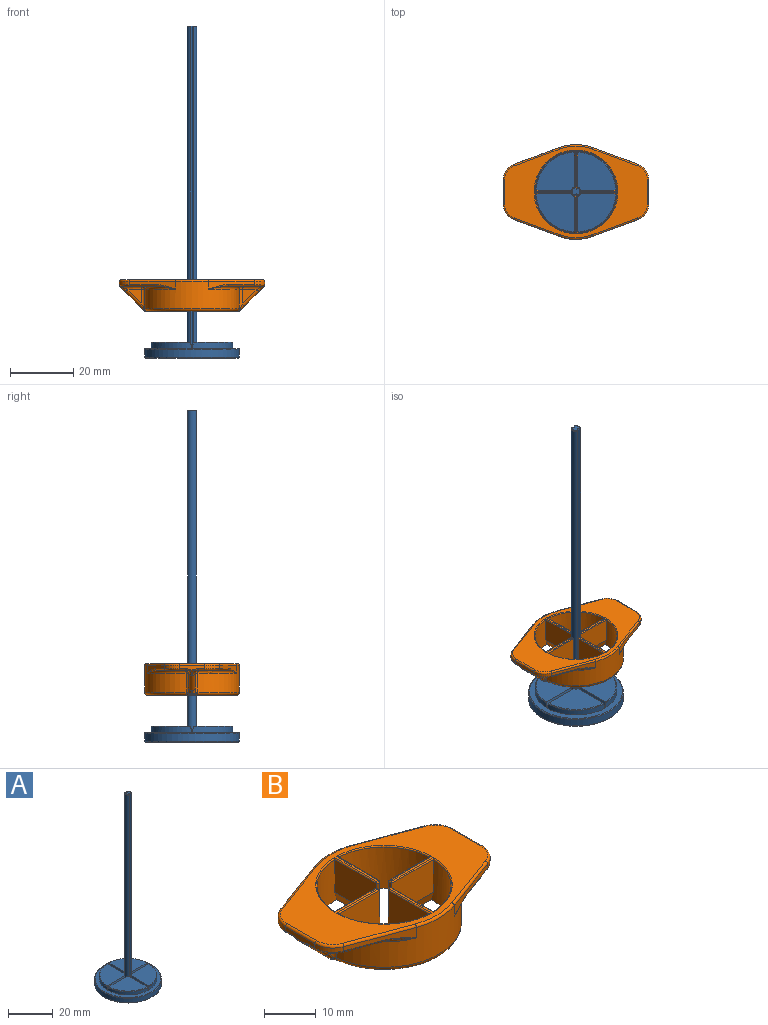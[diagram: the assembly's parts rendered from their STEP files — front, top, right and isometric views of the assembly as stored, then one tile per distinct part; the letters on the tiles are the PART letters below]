
ASSEMBLY  parts=2 mates=1
PART A: 44 faces, bbox 32.5x32.5x105 mm
  f0: cylinder r=15mm len=30mm, axis (0,0,-1), area 235.6mm2, adj f36,f43
  f1: plane 12.14x12.14mm, normal (0,0,1), area 112.7mm2, adj f8,f9,f14,f20,f32
  f2: plane 12.14x12.14mm, normal (0,0,1), area 112.7mm2, adj f6,f13,f15,f21,f34
  f3: plane 12.14x12.14mm, normal (0,0,1), area 112.7mm2, adj f5,f6,f17,f22,f35
  f4: plane 12.14x12.14mm, normal (0,0,1), area 112.7mm2, adj f9,f10,f18,f19,f33
  f5: plane 101.75x0.55mm, normal (0.71,0.71,0), area 78.7mm2, adj f3,f6,f10,f17,f38
  f6: cylinder r=1.5mm len=101.75mm, axis (0,0,-1), area 358.2mm2, adj f2,f3,f5,f7,f21,f22,f40
  f7: plane 103.75x0.55mm, normal (0.71,-0.71,0), area 79mm2, adj f6,f8,f13,f15,f16,f28,f42
  f8: plane 101.75x0.55mm, normal (-0.71,-0.71,0), area 78.7mm2, adj f1,f7,f9,f14,f41
  f9: cylinder r=1.5mm len=101.75mm, axis (0,0,-1), area 358.2mm2, adj f1,f4,f8,f10,f19,f20,f39
  f10: plane 101.75x0.55mm, normal (-0.71,0.71,0), area 78.7mm2, adj f4,f5,f9,f18,f37
  f11: plane 2.5x2.19mm, normal (0,0,1), area 3.9mm2, adj f37,f38,f39,f40,f41,f42
  f12: plane 29.5x29.5mm, normal (0,0,-1), area 140.2mm2, adj f30,f43
  f13: plane 12.06x2mm, normal (0.97,0,0.24), area 24.3mm2, adj f2,f7,f14,f16,f26,f34
  f14: plane 12.06x2mm, normal (-0.97,0,0.24), area 24.3mm2, adj f1,f8,f13,f24,f32
  f15: cylinder r=1.5mm len=4mm, axis (0,0,-1), area 0.2mm2, adj f2,f7,f16,f28
  f16: plane 4x0.07mm, normal (-1,0,0), area 0.3mm2, adj f7,f13,f15,f28
  f17: plane 12.06x2mm, normal (0.97,0,0.24), area 24.3mm2, adj f3,f5,f18,f25,f35
  f18: plane 12.06x2mm, normal (-0.97,0,0.24), area 24.3mm2, adj f4,f10,f17,f23,f33
  f19: plane 11.49x2mm, normal (0,-0.97,0.24), area 23.5mm2, adj f4,f9,f20,f23,f33
  f20: plane 11.49x2mm, normal (0,0.97,0.24), area 23.5mm2, adj f1,f9,f19,f24,f32
  f21: plane 11.49x2mm, normal (0,0.97,0.24), area 23.5mm2, adj f2,f6,f22,f26,f34
  f22: plane 11.49x2mm, normal (0,-0.97,0.24), area 23.5mm2, adj f3,f6,f21,f25,f35
  f23: cylinder r=12.9mm len=12.9mm, axis (0,0,-1), area 34.7mm2, adj f18,f19,f27,f33
  f24: cylinder r=12.9mm len=12.9mm, axis (0,0,-1), area 34.7mm2, adj f14,f20,f27,f32
  f25: cylinder r=12.9mm len=12.9mm, axis (0,0,-1), area 34.7mm2, adj f17,f22,f27,f35
  f26: cylinder r=12.9mm len=12.9mm, axis (0,0,-1), area 34.7mm2, adj f13,f21,f27,f34
  f27: plane 29.5x29.5mm, normal (0,0,1), area 160.7mm2, adj f23,f24,f25,f26,f36
  f28: plane 25.3x25.3mm, normal (0,0,-1), area 502.7mm2, adj f7,f15,f16,f31
  f29: cylinder r=12.9mm len=25.8mm, axis (0,0,-1), area 40.5mm2, adj f30,f31
  f30: torus R=13.15mm, axis (0,0,1), area 32.1mm2, adj f12,f29
  f31: torus R=12.65mm, axis (0,0,1), area 31.6mm2, adj f28,f29
  f32: torus R=12.65mm, axis (0,0,1), area 7.5mm2, adj f1,f14,f20,f24
  f33: torus R=12.65mm, axis (0,0,1), area 7.5mm2, adj f4,f18,f19,f23
  f34: torus R=12.65mm, axis (0,0,1), area 7.5mm2, adj f2,f13,f21,f26
  f35: torus R=12.65mm, axis (0,0,1), area 7.5mm2, adj f3,f17,f22,f25
  f36: torus R=14.75mm, axis (0,0,1), area 36.8mm2, adj f0,f27
  f37: cylinder r=0.25mm len=0.91mm, axis (0.71,0.71,0), area 0.3mm2, adj f10,f11,f38,f39
  f38: cylinder r=0.25mm len=0.91mm, axis (0.71,-0.71,0), area 0.3mm2, adj f5,f11,f37,f40
  f39: torus R=1.25mm, axis (0,0,1), area 1.3mm2, adj f9,f11,f37,f41
  f40: torus R=1.25mm, axis (0,0,1), area 1.3mm2, adj f6,f11,f38,f42
  f41: cylinder r=0.25mm len=0.91mm, axis (-0.71,0.71,0), area 0.3mm2, adj f8,f11,f39,f42
  f42: cylinder r=0.25mm len=0.91mm, axis (-0.71,-0.71,0), area 0.3mm2, adj f7,f11,f40,f41
  f43: torus R=14.75mm, axis (0,0,1), area 36.8mm2, adj f0,f12
PART B: 147 faces, bbox 47.2x34.3x10.4 mm
  f0: plane 1.57x1.56mm, normal (0.71,0,-0.71), area 1mm2, adj f1,f145,f146
  f1: bspline ~2.63x1.91mm, area 2.8mm2, adj f0,f2,f143,f144
  f2: cylinder r=1mm len=5.41mm, axis (-0.71,0,-0.71), area 20.9mm2, adj f1,f3,f140,f141,f142,f146
  f3: plane 4.7x4.68mm, normal (0,1,0), area 11mm2, adj f2,f4,f139
  f4: cylinder r=1mm len=6mm, axis (0,0,-1), area 8.2mm2, adj f3,f5,f137,f138,f140
  f5: torus R=2mm, axis (0,0,1), area 1.6mm2, adj f4,f6,f135,f136
  f6: plane 29.11x28mm, normal (0,0,-1), area 86.8mm2, adj f5,f7,f123,f124,f125,f126,f127,f129
  f7: cylinder r=13mm len=13mm, axis (0,0,-1), area 190.3mm2, adj f6,f8,f119,f120,f121,f122
  f8: plane 11.37x7.75mm, normal (-1,0,0), area 88.1mm2, adj f7,f9,f118,f122
  f9: cylinder r=0.25mm len=11.62mm, axis (0,1,0), area 4.5mm2, adj f8,f10,f117,f119
  f10: plane 45x29mm, normal (0,0,1), area 475.1mm2, adj f9,f11,f12,f16,f17,f18,f25,f26
  f11: cylinder r=0.25mm len=11.62mm, axis (-1,0,0), area 4.5mm2, adj f10,f12,f119,f120
  f12: torus R=1.95mm, axis (0,0,-1), area 0.3mm2, adj f10,f11,f13,f16
  f13: cylinder r=1.7mm len=9.75mm, axis (0,0,-1), area 8.9mm2, adj f12,f14,f15,f120,f121
  f14: plane 11.37x7.75mm, normal (0,-1,0), area 88.1mm2, adj f13,f15,f16,f125
  f15: plane 11.4x2.02mm, normal (0,-0.97,-0.24), area 23.3mm2, adj f13,f14,f121,f125
  f16: cylinder r=0.25mm len=11.62mm, axis (-1,0,0), area 4.5mm2, adj f10,f12,f14,f17
  f17: torus R=13.25mm, axis (0,0,-1), area 7.8mm2, adj f10,f16,f18,f125
  f18: cylinder r=0.25mm len=11.62mm, axis (0,1,0), area 4.5mm2, adj f10,f17,f19,f25
  f19: plane 11.37x7.75mm, normal (-1,0,0), area 88.1mm2, adj f18,f20,f24,f125
  f20: plane 11.88x2mm, normal (-0.97,0,-0.24), area 24mm2, adj f19,f21,f24,f125
  f21: plane 11.88x2mm, normal (0.97,0,-0.24), area 24mm2, adj f20,f22,f23,f124
  f22: plane 11.37x7.75mm, normal (1,0,0), area 88.1mm2, adj f21,f23,f27,f124
  f23: plane 9.75x0.5mm, normal (0.71,0.71,0), area 6.2mm2, adj f21,f22,f24,f26
  f24: plane 9.75x0.5mm, normal (-0.71,0.71,0), area 6.2mm2, adj f19,f20,f23,f25
  f25: cylinder r=0.25mm len=0.68mm, axis (-0.71,-0.71,0), area 0.2mm2, adj f10,f18,f24,f26
  f26: cylinder r=0.25mm len=0.68mm, axis (-0.71,0.71,0), area 0.2mm2, adj f10,f23,f25,f27
  f27: cylinder r=0.25mm len=11.62mm, axis (0,1,0), area 4.5mm2, adj f10,f22,f26,f28
  f28: torus R=13.25mm, axis (0,0,-1), area 7.8mm2, adj f10,f27,f29,f124
  f29: cylinder r=0.25mm len=11.62mm, axis (-1,0,0), area 4.5mm2, adj f10,f28,f30,f35
  f30: plane 11.37x7.75mm, normal (0,-1,0), area 88.1mm2, adj f29,f31,f34,f124
  f31: plane 11.4x2.02mm, normal (0,-0.97,-0.24), area 23.3mm2, adj f30,f32,f34,f124
  f32: plane 11.4x2.02mm, normal (0,0.97,-0.24), area 23.3mm2, adj f31,f33,f34,f123
  f33: plane 11.37x7.75mm, normal (0,1,0), area 88.1mm2, adj f32,f34,f36,f123
  f34: cylinder r=1.7mm len=9.75mm, axis (0,0,-1), area 8.9mm2, adj f30,f31,f32,f33,f35
  f35: torus R=1.95mm, axis (0,0,-1), area 0.3mm2, adj f10,f29,f34,f36
  f36: cylinder r=0.25mm len=11.62mm, axis (-1,0,0), area 4.5mm2, adj f10,f33,f35,f37
  f37: torus R=13.25mm, axis (0,0,-1), area 7.8mm2, adj f10,f36,f38,f123
  f38: cylinder r=0.25mm len=11.62mm, axis (0,1,0), area 4.5mm2, adj f10,f37,f39,f42
  f39: plane 11.37x7.75mm, normal (1,0,0), area 88.1mm2, adj f38,f40,f41,f123
  f40: plane 11.88x2mm, normal (0.97,0,-0.24), area 24mm2, adj f39,f41,f122,f123
  f41: plane 9.75x0.5mm, normal (0.71,-0.71,0), area 6.2mm2, adj f39,f40,f42,f118
  f42: cylinder r=0.25mm len=0.68mm, axis (0.71,0.71,0), area 0.2mm2, adj f10,f38,f41,f117
  f43: cylinder r=0.5mm len=14.71mm, axis (0.94,-0.35,0), area 12.2mm2, adj f10,f44,f106,f116
  f44: plane 14.91x5.74mm, normal (0.35,0.94,0), area 19.4mm2, adj f43,f45,f104,f105,f137
  f45: bspline ~6.35x2.81mm, area 1.7mm2, adj f44,f46,f104
  f46: torus R=16mm, axis (0,0,1), area 21mm2, adj f45,f47,f137,f138
  f47: plane 11.13x9.26mm, normal (0,0,-1), area 51.7mm2, adj f46,f48,f103,f104,f139
  f48: cylinder r=0.5mm len=2.02mm, axis (0,-1,0), area 1.6mm2, adj f47,f49,f51,f103
  f49: torus R=1.5mm, axis (-1,0,0), area 0.3mm2, adj f48,f50,f51,f139
  f50: bspline ~1.23x0.68mm, area 0.5mm2, adj f49,f51,f145,f146
  f51: plane 8.03x1.29mm, normal (1,0,0), area 8.8mm2, adj f48,f49,f50,f52,f53,f102,f105,f107
  f52: torus R=1.5mm, axis (-1,0,0), area 0.3mm2, adj f51,f53,f143,f144
  f53: cylinder r=0.5mm len=2.02mm, axis (0,-1,0), area 1.6mm2, adj f51,f52,f54,f101
  f54: plane 11.13x9.26mm, normal (0,0,-1), area 51.7mm2, adj f53,f55,f100,f101,f143
  f55: torus R=16mm, axis (0,0,1), area 21mm2, adj f54,f56,f58,f99
  f56: bspline ~6.35x2.81mm, area 1.7mm2, adj f55,f57,f100
  f57: plane 14.91x5.74mm, normal (0.35,-0.94,0), area 19.4mm2, adj f56,f58,f100,f102,f109
  f58: cylinder r=15mm len=29.76mm, axis (0,0,-1), area 286.7mm2, adj f55,f57,f59,f60,f97,f98,f110,f130
  f59: cylinder r=1mm len=6mm, axis (0,0,-1), area 8.2mm2, adj f58,f99,f131,f141,f142
  f60: cylinder r=1mm len=6mm, axis (0,0,-1), area 8.2mm2, adj f58,f61,f95,f96,f129
  f61: bspline ~2.52x1.82mm, area 2.2mm2, adj f60,f62,f63,f94
  f62: sphere r=1mm, area 0.4mm2, adj f61,f127,f129
  f63: plane 1.32x1.32mm, normal (-0.71,0,-0.71), area 0.6mm2, adj f61,f64,f127
  f64: bspline ~2.52x1.82mm, area 2.2mm2, adj f63,f65,f66,f94
  f65: sphere r=1mm, area 0.8mm2, adj f64,f126,f127
  f66: cylinder r=1mm len=6mm, axis (0,0,-1), area 8.2mm2, adj f64,f67,f93,f126,f137
  f67: plane 4.7x4.68mm, normal (0,1,0), area 11mm2, adj f66,f68,f94
  f68: cylinder r=1mm len=6.63mm, axis (-1,0,0), area 9.4mm2, adj f67,f69,f91,f92,f93
  f69: bspline ~2.63x1.91mm, area 2.8mm2, adj f68,f70,f90,f94
  f70: bspline ~1.22x0.68mm, area 0.5mm2, adj f69,f71,f89,f91
  f71: plane 8.03x1.29mm, normal (-1,0,0), area 8.8mm2, adj f70,f72,f79,f80,f81,f87,f88,f89
  f72: cylinder r=0.5mm len=2.02mm, axis (0,1,0), area 1.6mm2, adj f71,f73,f78,f79
  f73: plane 11.13x9.26mm, normal (0,0,-1), area 51.7mm2, adj f72,f74,f76,f78,f97
  f74: cylinder r=1mm len=6.63mm, axis (1,0,0), area 9.4mm2, adj f73,f75,f79,f95,f96
  f75: bspline ~2.63x1.91mm, area 2.8mm2, adj f74,f80,f90,f94
  f76: cylinder r=0.5mm len=8.37mm, axis (-0.94,0.35,0), area 6.9mm2, adj f73,f77,f78,f98
  f77: bspline ~6.35x2.81mm, area 1.7mm2, adj f76,f97,f98
  f78: torus R=4.5mm, axis (0,0,1), area 4.6mm2, adj f72,f73,f76,f88
  f79: torus R=1.5mm, axis (-1,0,0), area 0.3mm2, adj f71,f72,f74,f80
  f80: bspline ~1.23x0.68mm, area 0.5mm2, adj f71,f75,f79,f89
  f81: cylinder r=0.5mm len=2.02mm, axis (0,1,0), area 1.6mm2, adj f71,f82,f91,f92
  f82: torus R=4.5mm, axis (0,0,1), area 4.6mm2, adj f81,f83,f87,f92
  f83: cylinder r=0.5mm len=8.37mm, axis (0.94,0.35,0), area 6.9mm2, adj f82,f84,f86,f92
  f84: bspline ~6.35x2.81mm, area 1.7mm2, adj f83,f85,f86
  f85: torus R=16mm, axis (0,0,1), area 21mm2, adj f84,f92,f93,f137
  f86: plane 14.91x5.74mm, normal (-0.35,0.94,0), area 19.4mm2, adj f83,f84,f87,f115,f137
  f87: cylinder r=5mm len=4.69mm, axis (0,0,-1), area 6.1mm2, adj f71,f82,f86,f114
  f88: cylinder r=5mm len=4.69mm, axis (0,0,1), area 6.1mm2, adj f71,f78,f98,f112
  f89: cylinder r=0.5mm len=1.5mm, axis (0,1,0), area 0.6mm2, adj f70,f71,f80,f90
  f90: plane 1.57x1.56mm, normal (-0.71,0,-0.71), area 1mm2, adj f69,f75,f89
  f91: torus R=1.5mm, axis (-1,0,0), area 0.3mm2, adj f68,f70,f71,f81
  f92: plane 11.13x9.26mm, normal (0,0,-1), area 51.7mm2, adj f68,f81,f82,f83,f85
  f93: sphere r=1mm, area 2mm2, adj f66,f68,f85
  f94: cylinder r=1mm len=5.41mm, axis (0.71,0,-0.71), area 20.9mm2, adj f61,f64,f67,f69,f75,f96
  f95: sphere r=1mm, area 0.9mm2, adj f60,f74,f97
  f96: plane 4.7x4.68mm, normal (0,-1,0), area 11mm2, adj f60,f74,f94
  f97: torus R=16mm, axis (0,0,1), area 21mm2, adj f58,f73,f77,f95
  f98: plane 14.91x5.74mm, normal (-0.35,-0.94,0), area 19.4mm2, adj f58,f76,f77,f88,f111
  f99: sphere r=1mm, area 2mm2, adj f55,f59,f143
  f100: cylinder r=0.5mm len=8.37mm, axis (-0.94,-0.35,0), area 6.9mm2, adj f54,f56,f57,f101
  f101: torus R=4.5mm, axis (0,0,1), area 4.6mm2, adj f53,f54,f100,f102
  f102: cylinder r=5mm len=4.69mm, axis (0,0,1), area 6.1mm2, adj f51,f57,f101,f108
  f103: torus R=4.5mm, axis (0,0,1), area 4.6mm2, adj f47,f48,f104,f105
  f104: cylinder r=0.5mm len=8.37mm, axis (0.94,-0.35,0), area 6.9mm2, adj f44,f45,f47,f103
  f105: cylinder r=5mm len=4.69mm, axis (0,0,-1), area 6.1mm2, adj f44,f51,f103,f106
  f106: torus R=4.5mm, axis (0,0,-1), area 4.6mm2, adj f10,f43,f105,f107
  f107: cylinder r=0.5mm len=8.03mm, axis (0,-1,0), area 6.3mm2, adj f10,f51,f106,f108
  f108: torus R=4.5mm, axis (0,0,-1), area 4.6mm2, adj f10,f102,f107,f109
  f109: cylinder r=0.5mm len=14.71mm, axis (-0.94,-0.35,0), area 12.2mm2, adj f10,f57,f108,f110
  f110: torus R=14.5mm, axis (0,0,-1), area 8.2mm2, adj f10,f58,f109,f111
  f111: cylinder r=0.5mm len=14.71mm, axis (-0.94,0.35,0), area 12.2mm2, adj f10,f98,f110,f112
  f112: torus R=4.5mm, axis (0,0,-1), area 4.6mm2, adj f10,f88,f111,f113
  f113: cylinder r=0.5mm len=8.03mm, axis (0,1,0), area 6.3mm2, adj f10,f71,f112,f114
  f114: torus R=4.5mm, axis (0,0,-1), area 4.6mm2, adj f10,f87,f113,f115
  f115: cylinder r=0.5mm len=14.71mm, axis (0.94,0.35,0), area 12.2mm2, adj f10,f86,f114,f116
  f116: torus R=14.5mm, axis (0,0,-1), area 8.2mm2, adj f10,f43,f115,f137
  f117: cylinder r=0.25mm len=0.68mm, axis (0.71,-0.71,0), area 0.2mm2, adj f9,f10,f42,f118
  f118: plane 9.75x0.5mm, normal (-0.71,-0.71,0), area 6.2mm2, adj f8,f41,f117,f122
  f119: torus R=13.25mm, axis (0,0,-1), area 7.8mm2, adj f7,f9,f10,f11
  f120: plane 11.37x7.75mm, normal (0,1,0), area 88.1mm2, adj f7,f11,f13,f121
  f121: plane 11.4x2.02mm, normal (0,0.97,-0.24), area 23.3mm2, adj f7,f13,f15,f120
  f122: plane 11.88x2mm, normal (-0.97,0,-0.24), area 24mm2, adj f7,f8,f40,f118
  f123: cylinder r=13mm len=13mm, axis (0,0,-1), area 190.3mm2, adj f6,f32,f33,f37,f39,f40
  f124: cylinder r=13mm len=13mm, axis (0,0,-1), area 190.3mm2, adj f6,f21,f22,f28,f30,f31
  f125: cylinder r=13mm len=13mm, axis (0,0,-1), area 190.3mm2, adj f6,f14,f15,f17,f19,f20
  f126: torus R=2mm, axis (0,0,1), area 1.6mm2, adj f6,f65,f66,f136
  f127: cylinder r=1mm len=1mm, axis (0,-1,0), area 0.8mm2, adj f6,f62,f63,f65,f128
  f128: sphere r=1mm, area 0mm2, adj f127,f129
  f129: torus R=2mm, axis (0,0,1), area 1.6mm2, adj f6,f60,f62,f128,f130
  f130: torus R=14mm, axis (0,0,1), area 66.5mm2, adj f6,f58,f129,f131
  f131: torus R=2mm, axis (0,0,1), area 1.6mm2, adj f6,f59,f130,f132
  f132: sphere r=1mm, area 0.7mm2, adj f131,f133,f141
  f133: cylinder r=1mm len=1mm, axis (0,1,0), area 0.8mm2, adj f6,f132,f134,f135
  f134: plane 1.32x1.32mm, normal (0.71,0,-0.71), area 0.6mm2, adj f133,f140,f141
  f135: sphere r=1mm, area 0.5mm2, adj f5,f133,f140
  f136: torus R=14mm, axis (0,0,1), area 66.5mm2, adj f5,f6,f126,f137
  f137: cylinder r=15mm len=29.76mm, axis (0,0,-1), area 286.7mm2, adj f4,f44,f46,f66,f85,f86,f116,f136
  f138: sphere r=1mm, area 2.1mm2, adj f4,f46,f139
  f139: cylinder r=1mm len=6.63mm, axis (-1,0,0), area 9.4mm2, adj f3,f47,f49,f138,f146
  f140: bspline ~2.52x1.82mm, area 2.2mm2, adj f2,f4,f134,f135
  f141: bspline ~2.52x1.82mm, area 2.2mm2, adj f2,f59,f132,f134
  f142: plane 4.7x4.68mm, normal (0,-1,0), area 11mm2, adj f2,f59,f143
  f143: cylinder r=1mm len=6.63mm, axis (1,0,0), area 9.4mm2, adj f1,f52,f54,f99,f142
  f144: bspline ~1.23x0.68mm, area 0.5mm2, adj f1,f51,f52,f145
  f145: cylinder r=0.5mm len=1.5mm, axis (0,1,0), area 0.6mm2, adj f0,f50,f51,f144
  f146: bspline ~2.63x1.91mm, area 2.8mm2, adj f0,f2,f50,f139
PLACE A t=(0,0,-0.25)mm
PLACE B t=(0,0,14.5)mm
MATE slider A.f0 <-> B.f7  axis (0,0,-1) through (0,0,4.75)mm
